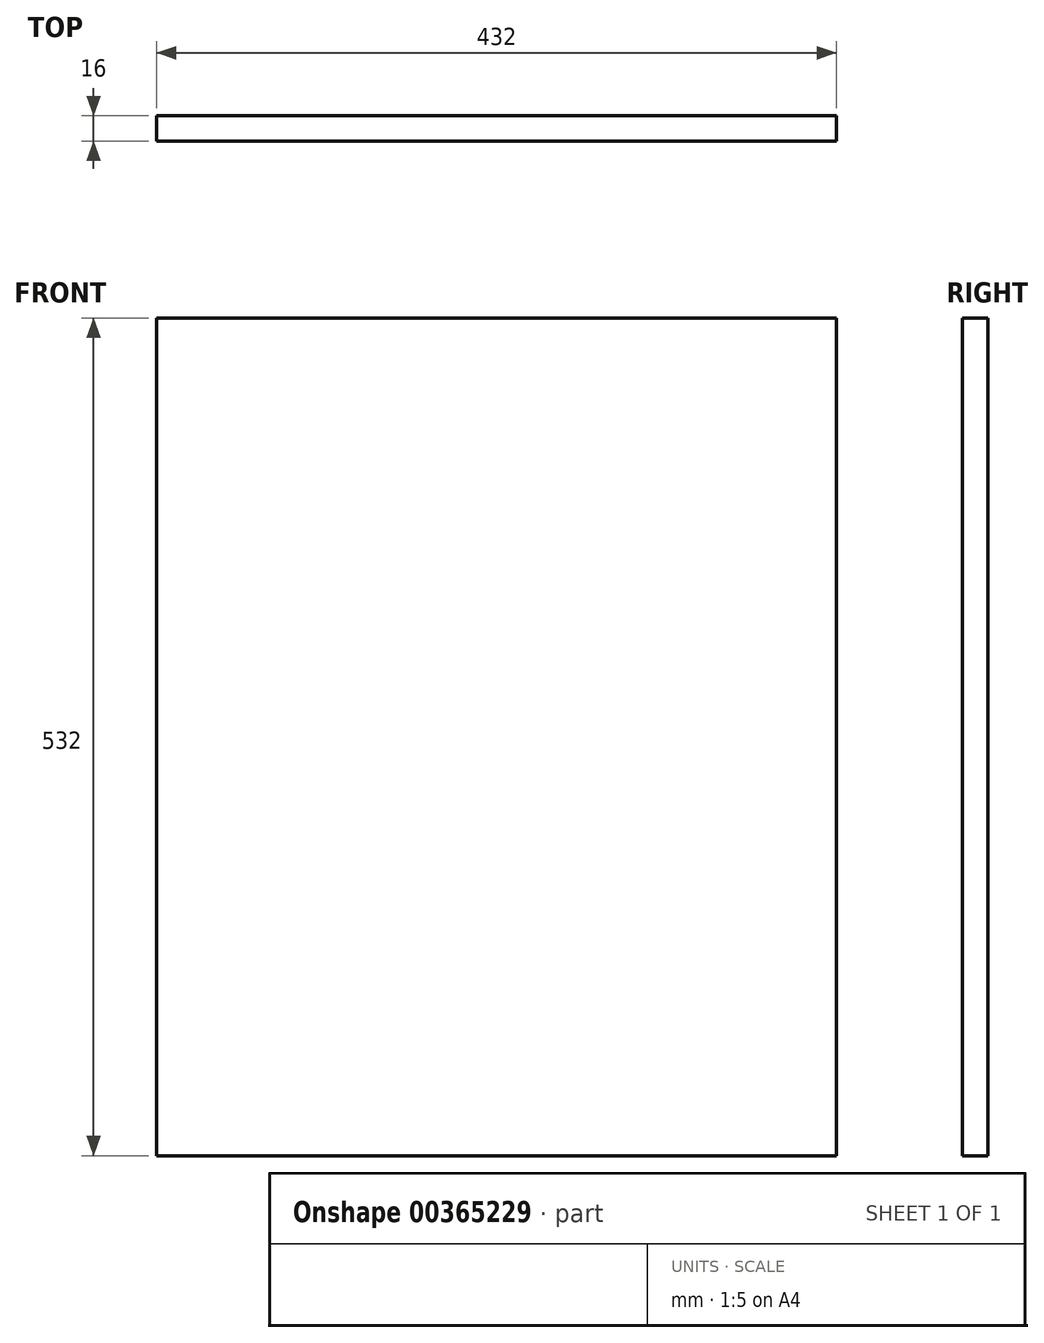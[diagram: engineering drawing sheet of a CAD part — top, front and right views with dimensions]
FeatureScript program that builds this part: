
annotation { "Feature Type Name" : "Feature", "Feature Type Description" : "" }
export const myFeature = defineFeature(function(context is Context, id is Id, definition is map)
    precondition{}
    {
        {
            var Q0;
            Q0=qCreatedBy(makeId("Front.planeOp"),FACE);
            var sketch = newSketch(context, id + "F0", { "sketchPlane" : qUnion([Q0])});
            skLineSegment(sketch, "E0.bottom", {"start": v(216, -266) * mm, "end": v(-216, -266) * mm});
            skLineSegment(sketch, "E0.top", {"start": v(216, 266) * mm, "end": v(-216, 266) * mm});
            skLineSegment(sketch, "E0.left", {"start": v(216, -266) * mm, "end": v(216, 266) * mm});
            skLineSegment(sketch, "E0.right", {"start": v(-216, -266) * mm, "end": v(-216, 266) * mm});
            skPoint(sketch, "E0.middle", {"position": v(0, 0) * mm});
            skSolve(sketch);
        }
        {
            var Q0;
            Q0 = qSketchRegion(id + "F0", true);
            extrude(context, id + "F1", {"entities" : qUnion([Q0]), "depth" : 16 * mm});
        }
    });
